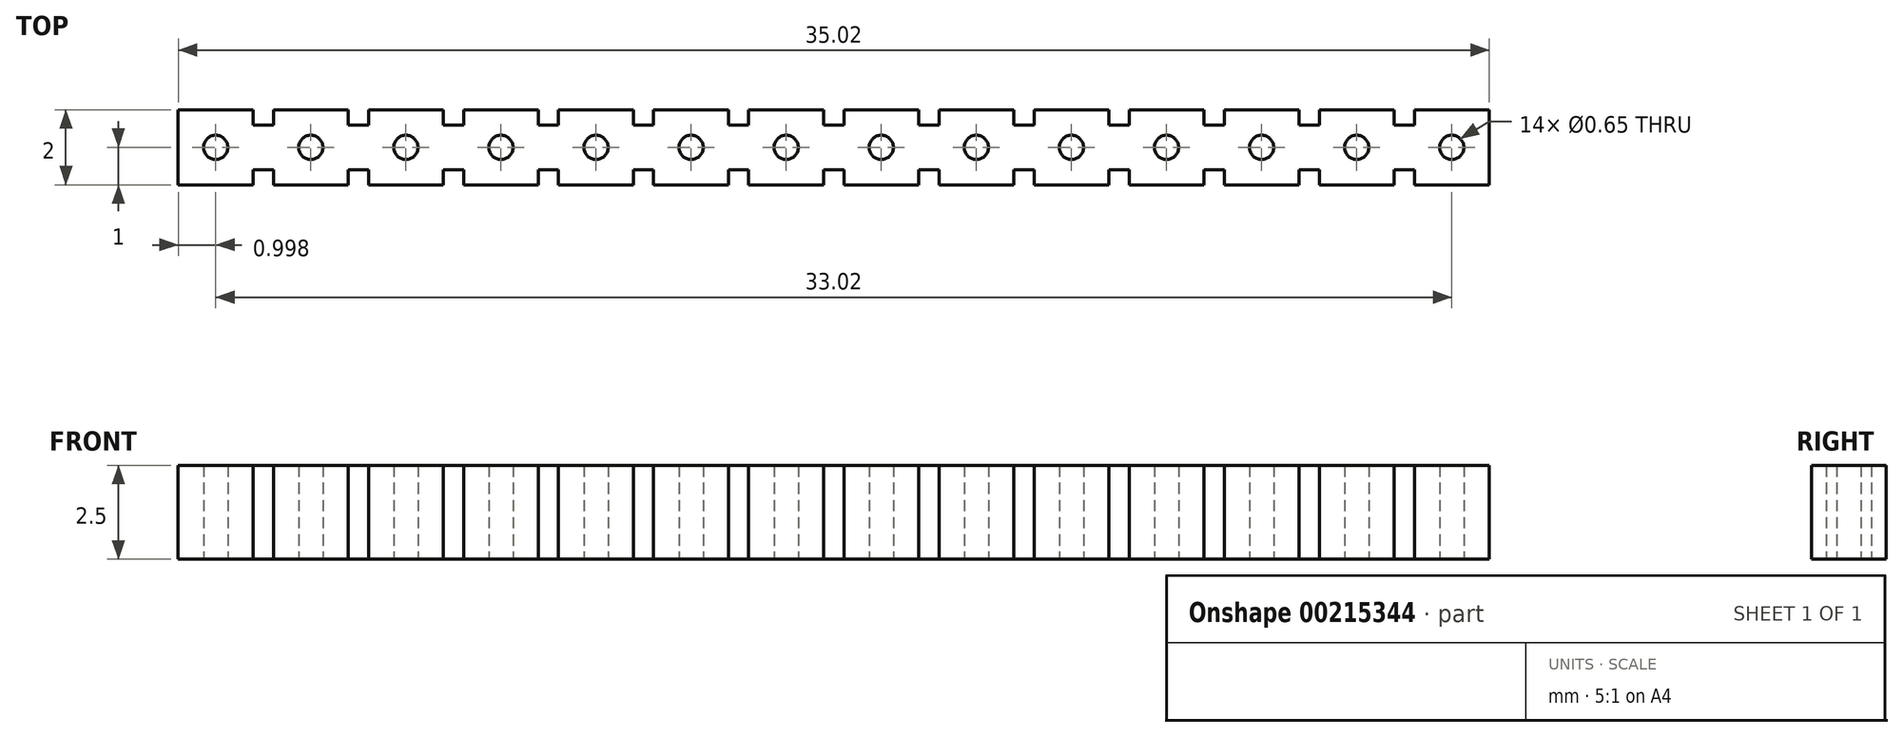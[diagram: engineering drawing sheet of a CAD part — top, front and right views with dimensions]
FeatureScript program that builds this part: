
annotation { "Feature Type Name" : "Feature", "Feature Type Description" : "" }
export const myFeature = defineFeature(function(context is Context, id is Id, definition is map)
    precondition{}
    {
        {
            var Q0;
            Q0=qCreatedBy(makeId("Top.planeOp"),FACE);
            var sketch = newSketch(context, id + "F0", { "sketchPlane" : qUnion([Q0])});
            skLineSegment(sketch, "E0.bottom", {"start": v(-69.27, 0) * mm, "end": v(-71.27, 0) * mm});
            skLineSegment(sketch, "E0.top", {"start": v(-69.27, 2) * mm, "end": v(-71.27, 2) * mm});
            skLineSegment(sketch, "E0.left", {"start": v(-69.27, 0) * mm, "end": v(-69.27, 2) * mm});
            skLineSegment(sketch, "E0.right", {"start": v(-71.27, 0) * mm, "end": v(-71.27, 2) * mm});
            skPoint(sketch, "E0.middle", {"position": v(-70.27, 1) * mm});
            skLineSegment(sketch, "E1.bottom", {"start": v(-69.27, 0.4) * mm, "end": v(-68.73, 0.4) * mm});
            skLineSegment(sketch, "E1.top", {"start": v(-69.27, 1.6) * mm, "end": v(-68.73, 1.6) * mm});
            skLineSegment(sketch, "E1.left", {"start": v(-69.27, 0.4) * mm, "end": v(-69.27, 1.6) * mm});
            skLineSegment(sketch, "E1.right", {"start": v(-68.73, 0.4) * mm, "end": v(-68.73, 1.6) * mm});
            skCircle(sketch, "E2", {"center": v(-70.27, 1) * mm, "radius": 0.33 * mm});
            skLineSegment(sketch, "E3.1.0.0", {"start": v(-66.73, 0.4) * mm, "end": v(-66.73, 1.6) * mm});
            skLineSegment(sketch, "E3.1.0.1", {"start": v(-66.73, 2) * mm, "end": v(-68.73, 2) * mm});
            skLineSegment(sketch, "E3.1.0.2", {"start": v(-66.2, 0.4) * mm, "end": v(-66.2, 1.6) * mm});
            skPoint(sketch, "E3.1.0.3", {"position": v(-67.73, 1) * mm});
            skLineSegment(sketch, "E3.1.0.4", {"start": v(-68.73, 0) * mm, "end": v(-68.73, 2) * mm});
            skCircle(sketch, "E3.1.0.5", {"center": v(-67.73, 1) * mm, "radius": 0.33 * mm});
            skLineSegment(sketch, "E3.1.0.6", {"start": v(-66.73, 0) * mm, "end": v(-66.73, 2) * mm});
            skLineSegment(sketch, "E3.1.0.7", {"start": v(-66.73, 0) * mm, "end": v(-68.73, 0) * mm});
            skLineSegment(sketch, "E3.1.0.8", {"start": v(-66.73, 1.6) * mm, "end": v(-66.2, 1.6) * mm});
            skLineSegment(sketch, "E3.1.0.9", {"start": v(-66.73, 0.4) * mm, "end": v(-66.2, 0.4) * mm});
            skLineSegment(sketch, "E3.2.0.0", {"start": v(-64.2, 0.4) * mm, "end": v(-64.2, 1.6) * mm});
            skLineSegment(sketch, "E3.2.0.1", {"start": v(-64.2, 2) * mm, "end": v(-66.2, 2) * mm});
            skLineSegment(sketch, "E3.2.0.2", {"start": v(-63.65, 0.4) * mm, "end": v(-63.65, 1.6) * mm});
            skPoint(sketch, "E3.2.0.3", {"position": v(-65.2, 1) * mm});
            skLineSegment(sketch, "E3.2.0.4", {"start": v(-66.2, 0) * mm, "end": v(-66.2, 2) * mm});
            skCircle(sketch, "E3.2.0.5", {"center": v(-65.2, 1) * mm, "radius": 0.33 * mm});
            skLineSegment(sketch, "E3.2.0.6", {"start": v(-64.2, 0) * mm, "end": v(-64.2, 2) * mm});
            skLineSegment(sketch, "E3.2.0.7", {"start": v(-64.2, 0) * mm, "end": v(-66.2, 0) * mm});
            skLineSegment(sketch, "E3.2.0.8", {"start": v(-64.2, 1.6) * mm, "end": v(-63.65, 1.6) * mm});
            skLineSegment(sketch, "E3.2.0.9", {"start": v(-64.2, 0.4) * mm, "end": v(-63.65, 0.4) * mm});
            skLineSegment(sketch, "E3.3.0.0", {"start": v(-61.65, 0.4) * mm, "end": v(-61.65, 1.6) * mm});
            skLineSegment(sketch, "E3.3.0.1", {"start": v(-61.65, 2) * mm, "end": v(-63.65, 2) * mm});
            skLineSegment(sketch, "E3.3.0.2", {"start": v(-61.11, 0.4) * mm, "end": v(-61.11, 1.6) * mm});
            skPoint(sketch, "E3.3.0.3", {"position": v(-62.65, 1) * mm});
            skLineSegment(sketch, "E3.3.0.4", {"start": v(-63.65, 0) * mm, "end": v(-63.65, 2) * mm});
            skCircle(sketch, "E3.3.0.5", {"center": v(-62.65, 1) * mm, "radius": 0.33 * mm});
            skLineSegment(sketch, "E3.3.0.6", {"start": v(-61.65, 0) * mm, "end": v(-61.65, 2) * mm});
            skLineSegment(sketch, "E3.3.0.7", {"start": v(-61.65, 0) * mm, "end": v(-63.65, 0) * mm});
            skLineSegment(sketch, "E3.3.0.8", {"start": v(-61.65, 1.6) * mm, "end": v(-61.11, 1.6) * mm});
            skLineSegment(sketch, "E3.3.0.9", {"start": v(-61.65, 0.4) * mm, "end": v(-61.11, 0.4) * mm});
            skLineSegment(sketch, "E3.4.0.0", {"start": v(-59.11, 0.4) * mm, "end": v(-59.11, 1.6) * mm});
            skLineSegment(sketch, "E3.4.0.1", {"start": v(-59.11, 2) * mm, "end": v(-61.11, 2) * mm});
            skLineSegment(sketch, "E3.4.0.2", {"start": v(-58.57, 0.4) * mm, "end": v(-58.57, 1.6) * mm});
            skPoint(sketch, "E3.4.0.3", {"position": v(-60.11, 1) * mm});
            skLineSegment(sketch, "E3.4.0.4", {"start": v(-61.11, 0) * mm, "end": v(-61.11, 2) * mm});
            skCircle(sketch, "E3.4.0.5", {"center": v(-60.11, 1) * mm, "radius": 0.33 * mm});
            skLineSegment(sketch, "E3.4.0.6", {"start": v(-59.11, 0) * mm, "end": v(-59.11, 2) * mm});
            skLineSegment(sketch, "E3.4.0.7", {"start": v(-59.11, 0) * mm, "end": v(-61.11, 0) * mm});
            skLineSegment(sketch, "E3.4.0.8", {"start": v(-59.11, 1.6) * mm, "end": v(-58.57, 1.6) * mm});
            skLineSegment(sketch, "E3.4.0.9", {"start": v(-59.11, 0.4) * mm, "end": v(-58.57, 0.4) * mm});
            skLineSegment(sketch, "E3.5.0.0", {"start": v(-56.57, 0.4) * mm, "end": v(-56.57, 1.6) * mm});
            skLineSegment(sketch, "E3.5.0.1", {"start": v(-56.57, 2) * mm, "end": v(-58.57, 2) * mm});
            skLineSegment(sketch, "E3.5.0.2", {"start": v(-56.03, 0.4) * mm, "end": v(-56.03, 1.6) * mm});
            skPoint(sketch, "E3.5.0.3", {"position": v(-57.57, 1) * mm});
            skLineSegment(sketch, "E3.5.0.4", {"start": v(-58.57, 0) * mm, "end": v(-58.57, 2) * mm});
            skCircle(sketch, "E3.5.0.5", {"center": v(-57.57, 1) * mm, "radius": 0.33 * mm});
            skLineSegment(sketch, "E3.5.0.6", {"start": v(-56.57, 0) * mm, "end": v(-56.57, 2) * mm});
            skLineSegment(sketch, "E3.5.0.7", {"start": v(-56.57, 0) * mm, "end": v(-58.57, 0) * mm});
            skLineSegment(sketch, "E3.5.0.8", {"start": v(-56.57, 1.6) * mm, "end": v(-56.03, 1.6) * mm});
            skLineSegment(sketch, "E3.5.0.9", {"start": v(-56.57, 0.4) * mm, "end": v(-56.03, 0.4) * mm});
            skLineSegment(sketch, "E3.6.0.0", {"start": v(-54.03, 0.4) * mm, "end": v(-54.03, 1.6) * mm});
            skLineSegment(sketch, "E3.6.0.1", {"start": v(-54.03, 2) * mm, "end": v(-56.03, 2) * mm});
            skLineSegment(sketch, "E3.6.0.2", {"start": v(-53.5, 0.4) * mm, "end": v(-53.5, 1.6) * mm});
            skPoint(sketch, "E3.6.0.3", {"position": v(-55.03, 1) * mm});
            skLineSegment(sketch, "E3.6.0.4", {"start": v(-56.03, 0) * mm, "end": v(-56.03, 2) * mm});
            skCircle(sketch, "E3.6.0.5", {"center": v(-55.03, 1) * mm, "radius": 0.33 * mm});
            skLineSegment(sketch, "E3.6.0.6", {"start": v(-54.03, 0) * mm, "end": v(-54.03, 2) * mm});
            skLineSegment(sketch, "E3.6.0.7", {"start": v(-54.03, 0) * mm, "end": v(-56.03, 0) * mm});
            skLineSegment(sketch, "E3.6.0.8", {"start": v(-54.03, 1.6) * mm, "end": v(-53.5, 1.6) * mm});
            skLineSegment(sketch, "E3.6.0.9", {"start": v(-54.03, 0.4) * mm, "end": v(-53.5, 0.4) * mm});
            skLineSegment(sketch, "E3.7.0.0", {"start": v(-51.5, 0.4) * mm, "end": v(-51.5, 1.6) * mm});
            skLineSegment(sketch, "E3.7.0.1", {"start": v(-51.5, 2) * mm, "end": v(-53.5, 2) * mm});
            skLineSegment(sketch, "E3.7.0.2", {"start": v(-50.95, 0.4) * mm, "end": v(-50.95, 1.6) * mm});
            skPoint(sketch, "E3.7.0.3", {"position": v(-52.5, 1) * mm});
            skLineSegment(sketch, "E3.7.0.4", {"start": v(-53.5, 0) * mm, "end": v(-53.5, 2) * mm});
            skCircle(sketch, "E3.7.0.5", {"center": v(-52.5, 1) * mm, "radius": 0.33 * mm});
            skLineSegment(sketch, "E3.7.0.6", {"start": v(-51.5, 0) * mm, "end": v(-51.5, 2) * mm});
            skLineSegment(sketch, "E3.7.0.7", {"start": v(-51.5, 0) * mm, "end": v(-53.5, 0) * mm});
            skLineSegment(sketch, "E3.7.0.8", {"start": v(-51.5, 1.6) * mm, "end": v(-50.95, 1.6) * mm});
            skLineSegment(sketch, "E3.7.0.9", {"start": v(-51.5, 0.4) * mm, "end": v(-50.95, 0.4) * mm});
            skLineSegment(sketch, "E3.8.0.0", {"start": v(-48.95, 0.4) * mm, "end": v(-48.95, 1.6) * mm});
            skLineSegment(sketch, "E3.8.0.1", {"start": v(-48.95, 2) * mm, "end": v(-50.95, 2) * mm});
            skLineSegment(sketch, "E3.8.0.2", {"start": v(-48.41, 0.4) * mm, "end": v(-48.41, 1.6) * mm});
            skPoint(sketch, "E3.8.0.3", {"position": v(-49.95, 1) * mm});
            skLineSegment(sketch, "E3.8.0.4", {"start": v(-50.95, 0) * mm, "end": v(-50.95, 2) * mm});
            skCircle(sketch, "E3.8.0.5", {"center": v(-49.95, 1) * mm, "radius": 0.33 * mm});
            skLineSegment(sketch, "E3.8.0.6", {"start": v(-48.95, 0) * mm, "end": v(-48.95, 2) * mm});
            skLineSegment(sketch, "E3.8.0.7", {"start": v(-48.95, 0) * mm, "end": v(-50.95, 0) * mm});
            skLineSegment(sketch, "E3.8.0.8", {"start": v(-48.95, 1.6) * mm, "end": v(-48.41, 1.6) * mm});
            skLineSegment(sketch, "E3.8.0.9", {"start": v(-48.95, 0.4) * mm, "end": v(-48.41, 0.4) * mm});
            skLineSegment(sketch, "E3.9.0.0", {"start": v(-46.41, 0.4) * mm, "end": v(-46.41, 1.6) * mm});
            skLineSegment(sketch, "E3.9.0.1", {"start": v(-46.41, 2) * mm, "end": v(-48.41, 2) * mm});
            skLineSegment(sketch, "E3.9.0.2", {"start": v(-45.87, 0.4) * mm, "end": v(-45.87, 1.6) * mm});
            skPoint(sketch, "E3.9.0.3", {"position": v(-47.41, 1) * mm});
            skLineSegment(sketch, "E3.9.0.4", {"start": v(-48.41, 0) * mm, "end": v(-48.41, 2) * mm});
            skCircle(sketch, "E3.9.0.5", {"center": v(-47.41, 1) * mm, "radius": 0.33 * mm});
            skLineSegment(sketch, "E3.9.0.6", {"start": v(-46.41, 0) * mm, "end": v(-46.41, 2) * mm});
            skLineSegment(sketch, "E3.9.0.7", {"start": v(-46.41, 0) * mm, "end": v(-48.41, 0) * mm});
            skLineSegment(sketch, "E3.9.0.8", {"start": v(-46.41, 1.6) * mm, "end": v(-45.87, 1.6) * mm});
            skLineSegment(sketch, "E3.9.0.9", {"start": v(-46.41, 0.4) * mm, "end": v(-45.87, 0.4) * mm});
            skLineSegment(sketch, "E3.10.0.0", {"start": v(-43.87, 0.4) * mm, "end": v(-43.87, 1.6) * mm});
            skLineSegment(sketch, "E3.10.0.1", {"start": v(-43.87, 2) * mm, "end": v(-45.87, 2) * mm});
            skLineSegment(sketch, "E3.10.0.2", {"start": v(-43.33, 0.4) * mm, "end": v(-43.33, 1.6) * mm});
            skPoint(sketch, "E3.10.0.3", {"position": v(-44.87, 1) * mm});
            skLineSegment(sketch, "E3.10.0.4", {"start": v(-45.87, 0) * mm, "end": v(-45.87, 2) * mm});
            skCircle(sketch, "E3.10.0.5", {"center": v(-44.87, 1) * mm, "radius": 0.33 * mm});
            skLineSegment(sketch, "E3.10.0.6", {"start": v(-43.87, 0) * mm, "end": v(-43.87, 2) * mm});
            skLineSegment(sketch, "E3.10.0.7", {"start": v(-43.87, 0) * mm, "end": v(-45.87, 0) * mm});
            skLineSegment(sketch, "E3.10.0.8", {"start": v(-43.87, 1.6) * mm, "end": v(-43.33, 1.6) * mm});
            skLineSegment(sketch, "E3.10.0.9", {"start": v(-43.87, 0.4) * mm, "end": v(-43.33, 0.4) * mm});
            skLineSegment(sketch, "E3.11.0.0", {"start": v(-41.33, 0.4) * mm, "end": v(-41.33, 1.6) * mm});
            skLineSegment(sketch, "E3.11.0.1", {"start": v(-41.33, 2) * mm, "end": v(-43.33, 2) * mm});
            skLineSegment(sketch, "E3.11.0.2", {"start": v(-40.8, 0.4) * mm, "end": v(-40.8, 1.6) * mm});
            skPoint(sketch, "E3.11.0.3", {"position": v(-42.33, 1) * mm});
            skLineSegment(sketch, "E3.11.0.4", {"start": v(-43.33, 0) * mm, "end": v(-43.33, 2) * mm});
            skCircle(sketch, "E3.11.0.5", {"center": v(-42.33, 1) * mm, "radius": 0.33 * mm});
            skLineSegment(sketch, "E3.11.0.6", {"start": v(-41.33, 0) * mm, "end": v(-41.33, 2) * mm});
            skLineSegment(sketch, "E3.11.0.7", {"start": v(-41.33, 0) * mm, "end": v(-43.33, 0) * mm});
            skLineSegment(sketch, "E3.11.0.8", {"start": v(-41.33, 1.6) * mm, "end": v(-40.8, 1.6) * mm});
            skLineSegment(sketch, "E3.11.0.9", {"start": v(-41.33, 0.4) * mm, "end": v(-40.8, 0.4) * mm});
            skLineSegment(sketch, "E3.12.0.0", {"start": v(-38.8, 0.4) * mm, "end": v(-38.8, 1.6) * mm});
            skLineSegment(sketch, "E3.12.0.1", {"start": v(-38.8, 2) * mm, "end": v(-40.8, 2) * mm});
            skLineSegment(sketch, "E3.12.0.2", {"start": v(-38.25, 0.4) * mm, "end": v(-38.25, 1.6) * mm});
            skPoint(sketch, "E3.12.0.3", {"position": v(-39.8, 1) * mm});
            skLineSegment(sketch, "E3.12.0.4", {"start": v(-40.8, 0) * mm, "end": v(-40.8, 2) * mm});
            skCircle(sketch, "E3.12.0.5", {"center": v(-39.8, 1) * mm, "radius": 0.33 * mm});
            skLineSegment(sketch, "E3.12.0.6", {"start": v(-38.8, 0) * mm, "end": v(-38.8, 2) * mm});
            skLineSegment(sketch, "E3.12.0.7", {"start": v(-38.8, 0) * mm, "end": v(-40.8, 0) * mm});
            skLineSegment(sketch, "E3.12.0.8", {"start": v(-38.8, 1.6) * mm, "end": v(-38.25, 1.6) * mm});
            skLineSegment(sketch, "E3.12.0.9", {"start": v(-38.8, 0.4) * mm, "end": v(-38.25, 0.4) * mm});
            skLineSegment(sketch, "E3.13.0.0", {"start": v(-36.25, 0.4) * mm, "end": v(-36.25, 1.6) * mm});
            skLineSegment(sketch, "E3.13.0.1", {"start": v(-36.25, 2) * mm, "end": v(-38.25, 2) * mm});
            skPoint(sketch, "E3.13.0.3", {"position": v(-37.25, 1) * mm});
            skLineSegment(sketch, "E3.13.0.4", {"start": v(-38.25, 0) * mm, "end": v(-38.25, 2) * mm});
            skCircle(sketch, "E3.13.0.5", {"center": v(-37.25, 1) * mm, "radius": 0.33 * mm});
            skLineSegment(sketch, "E3.13.0.6", {"start": v(-36.25, 0) * mm, "end": v(-36.25, 2) * mm});
            skLineSegment(sketch, "E3.13.0.7", {"start": v(-36.25, 0) * mm, "end": v(-38.25, 0) * mm});
            skLineSegment(sketch, "E3.direction1", {"start": v(-71.27, 0) * mm, "end": v(-68.73, 0) * mm, "construction": true});
            skSolve(sketch);
        }
        {
            var Q0;
            Q0=qSketchRegion(id+"F0",true);
            extrude(context, id + "F1", {"entities" : qUnion([Q0]), "depth" : 2.5 * mm});
        }
    });
